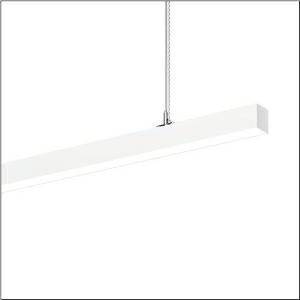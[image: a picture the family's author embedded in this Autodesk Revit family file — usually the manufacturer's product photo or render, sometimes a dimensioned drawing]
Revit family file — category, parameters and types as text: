
# Revit family: silica_21_51mx30dc39wb
name_source: partatom
category: Lighting Fixtures
units: mm (PartAtom-declared; Revit-internal decimal feet)

## family parameters
Cut with Voids When Loaded = No
Host = Face
Light Source = No
Part Type = Normal
Room Calculation Point = No
Round Connector Dimension = Use Diameter
Shared = No

## types (1)
- --- (1 x LED, 10520 lm, 68.3 W, 3000K)
    Apparent Load = 68 VA
    CIE Flux Codes = 47 79 96 57 100
    Color Rendering = 80
    Color Temperature = 3000K
    Default Elevation = 1800 mm
    Description = Silica 21, office luminaire, primary optical cover: cover, of PMMA, opal, light emission: direct/indirect distribution, primary light characteristic: symmetric, installation type: suspended mounting, LED, rated luminous flux: 10.520lm, luminous efficacy: 154lm/W, light colour: 830, colour temperature: 3000K, control gear: DALI 2, with terminal, 3+2-pole, max. 2.5mm², mains connection: 220..240V, AC, 50/60Hz, rated input power: 68.3W, luminaire housing, of aluminium, traffic white (RAL 9016), length: 3.004mm, width: 53mm, height: 53mm, protection rating (complete): IP20, insulation class (complete): insulation class I (protective earthing), certification: CE, permissible operating ambient temperature: 0..+35°C, standard: EN 50419, packaging unit: 1 piece
    Height = 53 mm
    Lamp = 1 x LED
    Lamp Light Flux = 10520 lm
    Lamp Power = 68.3 W
    Lamp count = 1
    Length = 3004 mm
    Luminous efficacy = 154 lm/W
    Manufacturer = Siteco
    ModVariant = No
    Model = 51MX30DC39WB
    Mounting Place = Ceiling
    Mounting Type = Pendant
    Number of Poles = 1
    OnlyDefault = Yes
    Power Factor = 1
    Product Name = Silica 21
    Product group = office luminaire | ceiling pendant
    ProductGroupID = 903
    Protection Class = Protection class I
    Protection Degree = IP 20
    RLX_Detail_Level = 1
    RLX_Emergency_Light_Flux = 0 lm
    RLX_Emergency_Type = 0
    RLX_Emergency_Type_DB = No
    RlxData = <blob elided: 20965 chars, md5=853b226d>
    Socket = socket
    Standby Power = 0 W
    System Light Flux = 10520 lm
    System Power = 68 W
    Type Comments = factory setting: luminous flux: 100 % | dim-lin: 254 | 233 mA
    Type Image = l_1349023.jpg
    URL = http://relux.com
    VarID = @adj_117557
    Voltage = 0 V
    Weight = 0.00 kg
    Width = 53 mm

## geometry (parser evidence)
native form markers: Blend x4, Sweep x12
no freeform markers — native parametric forms only
